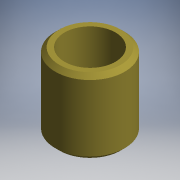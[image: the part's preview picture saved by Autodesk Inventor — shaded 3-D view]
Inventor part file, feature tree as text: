
AUTODESK INVENTOR PART (.ipt)
format: ipt  version: 2017.3 (Build 213256000, 256)  size: 105,472 bytes
history: native  units: mm (DEFAULTED — no unit token found)
features: other x35, revolve x1, sketch x1
ambient origin geometry x8: Origin, YZ Plane, XZ Plane, XY Plane, X Axis, Y Axis, Z Axis, Center Point
bodies: Solid1 (feature_tree)
feature tree (37):
  revolve  "Revolution1"  [1 undecoded]
  other  "bushing_XY"
  other  "bushing_YZ"
  other  "bushing_ZX"
  other  "bushing_X"
  other  "bushing_Y"
  other  "bushing_Z"
  other  "bushing_Center"
  other  "id1_XY"
  other  "id1_YZ"
  other  "id1_ZX"
  other  "id1_X"
  other  "id1_Y"
  other  "id1_Z"
  other  "id1_Center"
  other  "id2_XY"
  other  "id2_YZ"
  other  "id2_ZX"
  other  "id2_X"
  other  "id2_Y"
  other  "id2_Z"
  other  "id2_Center"
  other  "id3_XY"
  other  "id3_YZ"
  other  "id3_ZX"
  other  "id3_X"
  other  "id3_Y"
  other  "id3_Z"
  other  "id3_Center"
  other  "id4_XY"
  other  "id4_YZ"
  other  "id4_ZX"
  other  "id4_X"
  other  "id4_Y"
  other  "id4_Z"
  other  "id4_Center"
  sketch  "Sketch_1"  dims[d0=360.0deg d1=0.0mm d2=0.0mm]
note: 1 required parameter value undecoded (feature->parameter linkage not recoverable at this tier; creation-order binding heuristic only, values carry confidence <= 0.55)
